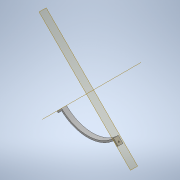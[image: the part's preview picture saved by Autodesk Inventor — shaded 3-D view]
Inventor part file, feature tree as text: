
AUTODESK INVENTOR PART (.ipt)
format: ipt  version: 2021 (Build 250183000, 183)  size: 201,728 bytes
history: native  units: in
note: dims shown in document units (in); Inventor stores cm internally (conversion verified against a paired STEP export)
features: sketch x8, extrude x6, hole x2, plane x2, split x2, pattern_circular x1
ambient origin geometry x8: Origin, YZ Plane, XZ Plane, XY Plane, X Axis, Y Axis, Z Axis, Center Point
bodies: Solid1 (feature_tree)
feature tree (21):
  extrude  "Extrusion1"  Depth=0.75in TaperAngle=0.0deg
  extrude  "Extrusion2"  TaperAngle=0.0deg  [1 undecoded]
  extrude  "Extrusion3"  TaperAngle=45.0deg  [1 undecoded]
  extrude  "Extrusion4"  TaperAngle=45.0deg  [1 undecoded]
  sketch  "Sketch6"  dims[d47=0.25in d48=45.0deg]
  hole  "Hole2"  [1 undecoded]
  plane  "Work Plane1"
  plane  "Work Plane2"
  extrude  "Extrusion7"  Depth=0.25in TaperAngle=360.0deg
  hole  "Hole4"  [1 undecoded]
  pattern_circular  "Circular Pattern1"  [2 undecoded]
  extrude  "Extrusion8"  [1 undecoded]
  split  "Split1"
  split  "Split2"
  sketch  "Sketch1"  dims[d3=0.0in d7=0.75in d8=0.0in]
  sketch  "Sketch2"  dims[d9=1.5in d10=0.0in d22=0.0in]
  sketch  "Sketch5"  dims[d31=0.266in d32=0.75in d33=0.507in d34=0.25in d35=0.5635in d36=1.0in d37=0.8108in d45=45.0deg d46=-0.3092in]
  sketch  "Sketch7"  dims[d49=1.0in d50=135.0deg]
  sketch  "Sketch11"  dims[d51=0.75in d52=0.0in]
  sketch  "Sketch12"  dims[d53=0.201in d54=0.75in d55=0.507in d56=0.25in d57=0.5635in d58=1.0in d59=0.8108in d60=1.5748in d61=360.0deg]
  sketch  "Sketch13"  dims[d63=0.35in d64=0.1in d65=0.0in d66=0.0in]
note: 8 required parameter values undecoded (feature->parameter linkage not recoverable at this tier; creation-order binding heuristic only, values carry confidence <= 0.55)
